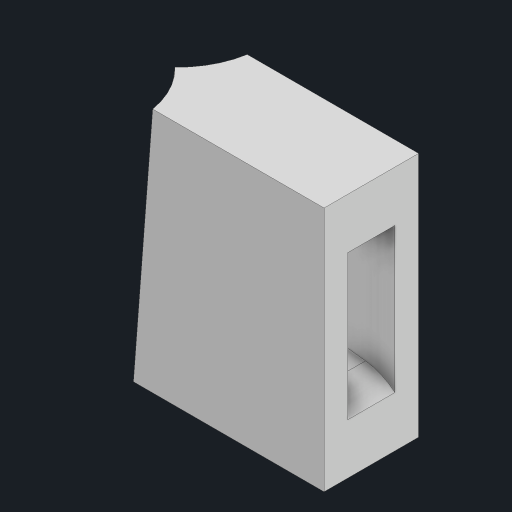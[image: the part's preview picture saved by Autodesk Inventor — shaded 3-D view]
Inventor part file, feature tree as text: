
AUTODESK INVENTOR PART (.ipt)
format: ipt  version: 2023.1 (Build 271208000, 208)  size: 165,376 bytes
history: native  units: mm
features: sketch x3, projected_geometry x2, plane x1, loft x1, extrude x1
ambient origin geometry x8: Origin, YZ Plane, XZ Plane, XY Plane, X Axis, Y Axis, Z Axis, Center Point
bodies: Body1 (feature_tree)
feature tree (8):
  sketch  "Sketch2"  dims[d0=13.0mm d2=0.5mm]
  plane  "Work Plane1"
  loft  "Loft1"
  extrude  "Extrusion2"  Depth=3.0mm
  sketch  "Sketch3"  dims[d4=0.5mm d5=3.0mm]
  sketch  "Sketch5"  dims[d6=10.0mm d8=20.0mm d9=0.5mm d11=8.0mm d16=17.0mm d17=0.5mm d18=0.0mm d19=90.0deg d20=0.0mm d21=90.0deg d26=26.0mm d27=4.401924mm d29=10.0mm d30=1.127387mm d31=1.127387mm d32=5.0mm d33=0.0mm d34=10.0mm d35=24.0mm d36=20.0mm d37=6.35mm d38=0.5mm]
  projected_geometry  "Projected Loop1"
  projected_geometry  "Projected Loop2"
